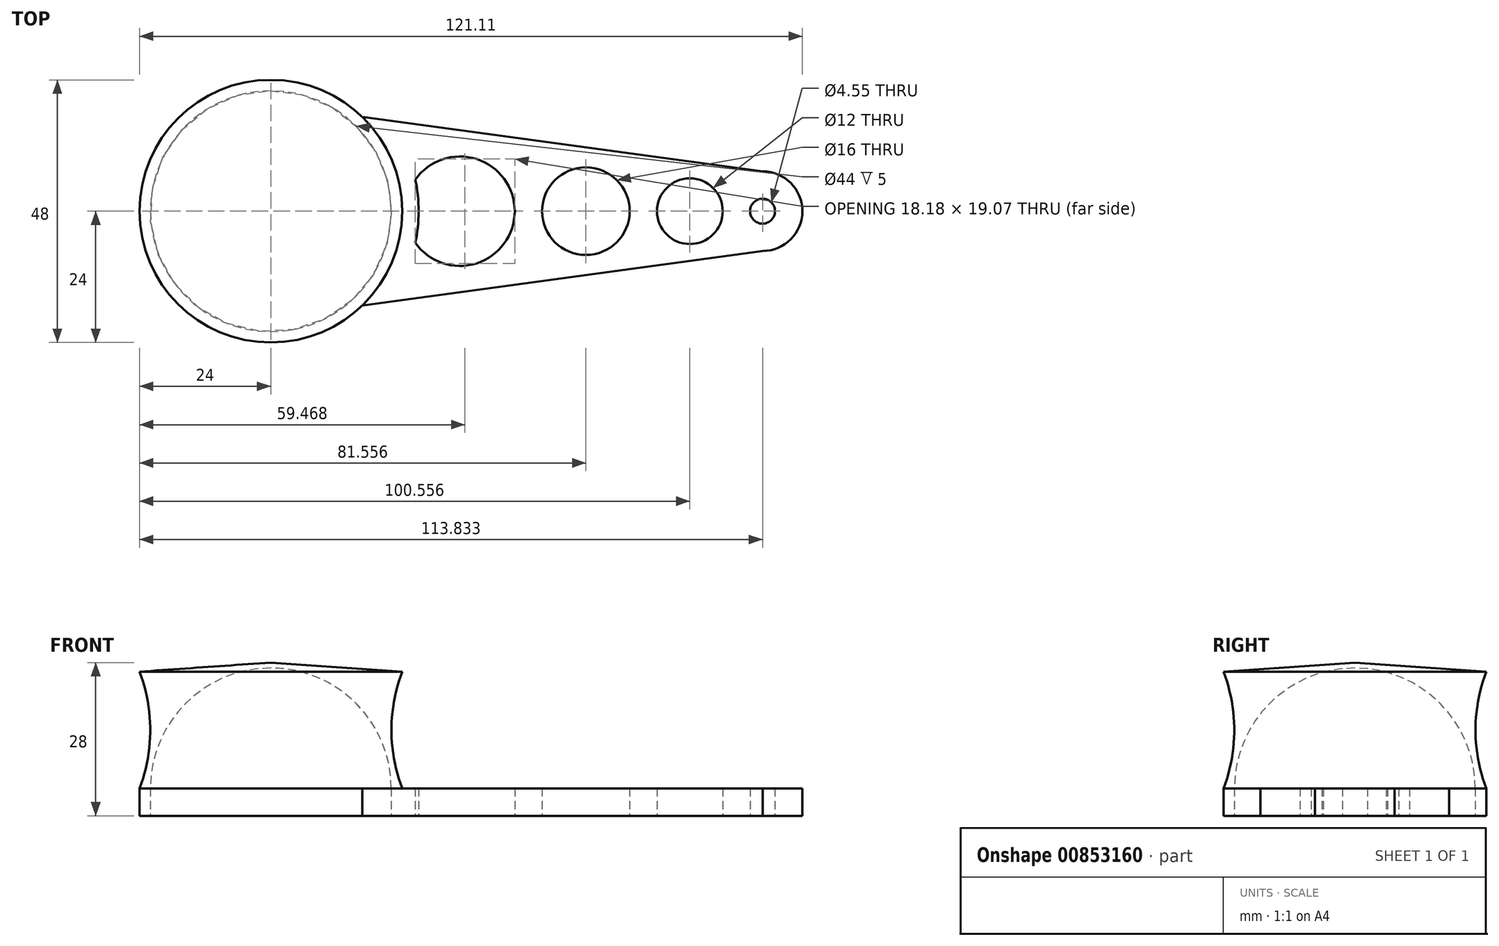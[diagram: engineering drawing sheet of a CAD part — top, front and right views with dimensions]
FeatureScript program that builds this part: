
annotation { "Feature Type Name" : "Feature", "Feature Type Description" : "" }
export const myFeature = defineFeature(function(context is Context, id is Id, definition is map)
    precondition{}
    {
        {
            var Q0;
            Q0=qCreatedBy(makeId("Top.planeOp"),FACE);
            var sketch = newSketch(context, id + "F0", { "sketchPlane" : qUnion([Q0])});
            skArc(sketch, "E0", {"start": v(89.83, -7.28) * mm, "mid": v(97.1, 0) * mm, "end": v(89.83, 7.28) * mm});
            skLineSegment(sketch, "E1", {"start": v(16.71, -17.23) * mm, "end": v(89.83, -7.28) * mm});
            skLineSegment(sketch, "E2", {"start": v(16.71, 17.23) * mm, "end": v(89.83, 7.28) * mm});
            skCircle(sketch, "E3", {"center": v(89.83, 0) * mm, "radius": 2.28 * mm});
            skCircle(sketch, "E4", {"center": v(76.56, 0) * mm, "radius": 6 * mm});
            skCircle(sketch, "E5", {"center": v(57.56, 0) * mm, "radius": 8 * mm});
            skArc(sketch, "E6", {"start": v(26.38, -5.76) * mm, "mid": v(44.56, 0) * mm, "end": v(26.38, 5.76) * mm});
            skArc(sketch, "E7", {"start": v(26.38, -5.76) * mm, "mid": v(27, 0) * mm, "end": v(26.38, 5.76) * mm});
            skArc(sketch, "E8", {"start": v(16.71, 17.23) * mm, "mid": v(-24, 0) * mm, "end": v(16.71, -17.23) * mm});
            skCircle(sketch, "E9", {"center": v(0, 0) * mm, "radius": 22 * mm});
            skSolve(sketch);
        }
        {
            var Q0;
            Q0 = qSketchRegion(id + "F0", true);
            extrude(context, id + "F1", {"entities" : qUnion([Q0]), "depth" : 5 * mm, "offsetDistance" : 25 * mm});
        }
        {
            var Q0;
            Q0=qCreatedBy(makeId("Front.planeOp"),FACE);
            var sketch = newSketch(context, id + "F2", { "sketchPlane" : qUnion([Q0])});
            skArc(sketch, "E10", {"start": v(0, 27) * mm, "mid": v(-15.56, 20.56) * mm, "end": v(-22, 5) * mm});
            skLineSegment(sketch, "E11", {"start": v(-24, 5) * mm, "end": v(-22, 5) * mm});
            skLineSegment(sketch, "E12", {"start": v(0, 28) * mm, "end": v(0, 27) * mm});
            skLineSegment(sketch, "E13", {"start": v(0, 35.04) * mm, "end": v(0, -9.13) * mm});
            skLineSegment(sketch, "E14", {"start": v(0, 28) * mm, "end": v(-24, 26.34) * mm});
            skArc(sketch, "E15", {"start": v(-24, 5) * mm, "mid": v(-22.04, 15.67) * mm, "end": v(-24, 26.34) * mm});
            skSolve(sketch);
        }
        {
            var Q0;
            Q0 = qSketchRegion(id + "F2", true);
            var Q1;
            Q1=sQuery(id+"F2.wireOp",EDGE,"E13");
            revolve(context, id + "F3", {"operationType" : NewBodyOperationType.ADD, "surfaceOperationType" : NewSurfaceOperationType.NEW, "entities" : qUnion([Q0]), "axis" : qUnion([Q1]), "revolveType" : RevolveType.FULL});
        }
    });
